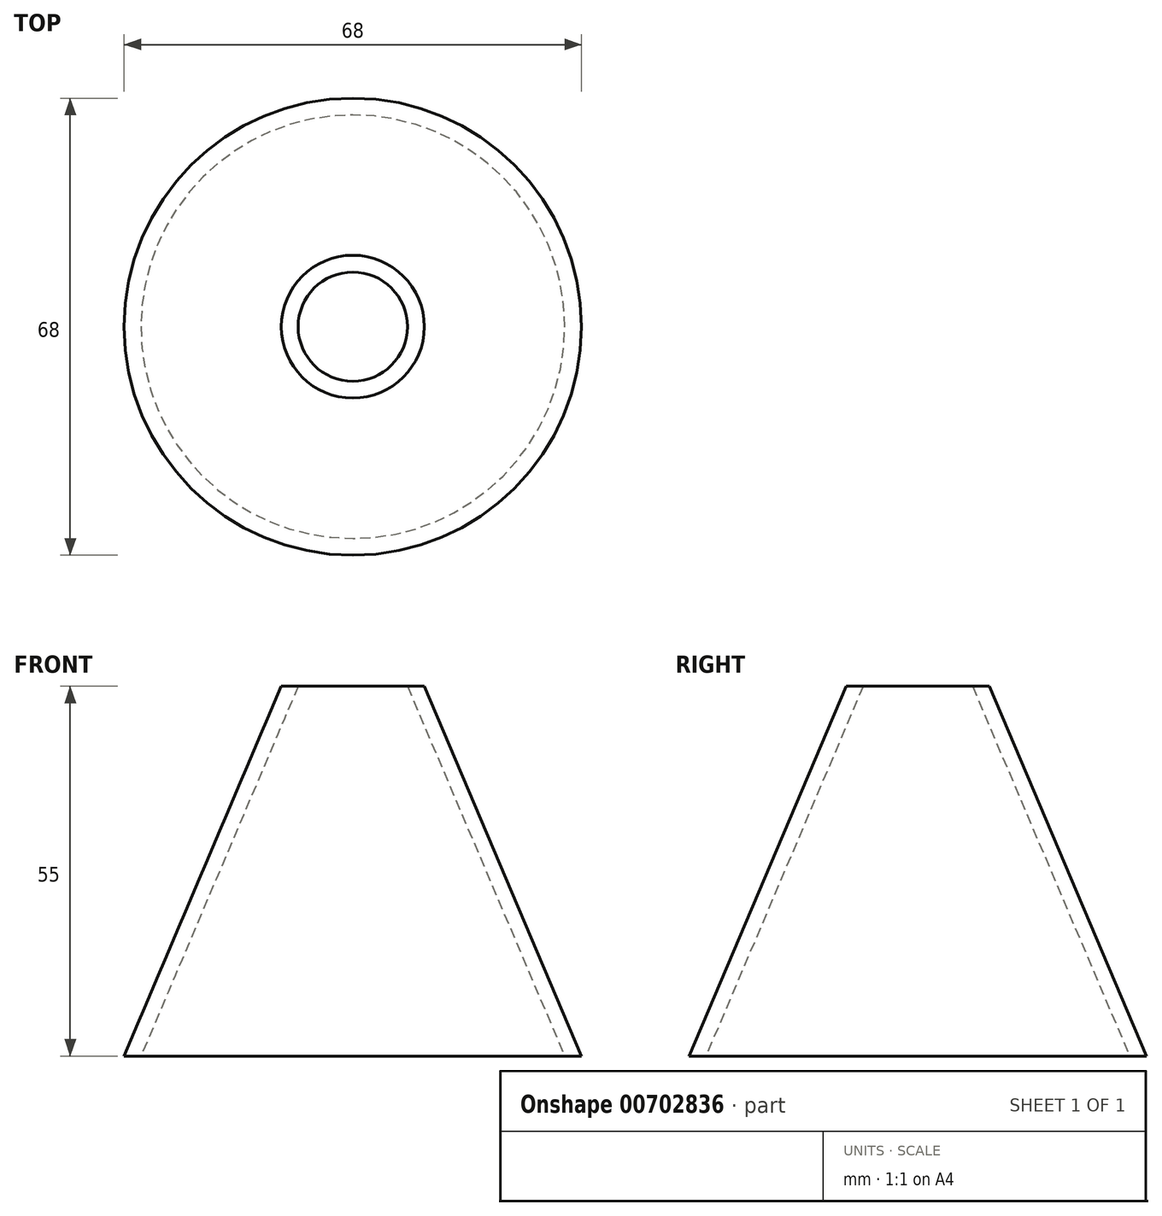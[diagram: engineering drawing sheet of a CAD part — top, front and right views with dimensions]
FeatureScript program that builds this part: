
annotation { "Feature Type Name" : "Feature", "Feature Type Description" : "" }
export const myFeature = defineFeature(function(context is Context, id is Id, definition is map)
    precondition{}
    {
        {
            var Q0;
            Q0=qCreatedBy(makeId("Front.planeOp"),FACE);
            var sketch = newSketch(context, id + "F0", { "sketchPlane" : qUnion([Q0])});
            skLineSegment(sketch, "E0", {"start": v(0, 80) * mm, "end": v(34, 0) * mm});
            skLineSegment(sketch, "E1", {"start": v(0, 80) * mm, "end": v(0, 0) * mm});
            skLineSegment(sketch, "E2", {"start": v(34, 0) * mm, "end": v(0, 0) * mm});
            skLineSegment(sketch, "E3", {"start": v(0, 55) * mm, "end": v(10.62, 55) * mm});
            skLineSegment(sketch, "E4", {"start": v(8.12, 55) * mm, "end": v(31.5, 0) * mm});
            skSolve(sketch);
        }
        {
            var Q0;
            {var subQ5=sQuery(id+"F0.wireOp",EDGE,"E4");Q0=makeQuery(id+"F0.imprint","IMPRINT",FACE,{"disambiguationData":[TD([[makeQuery(id+"F0.imprint","IMPRINT",EDGE,{"derivedFrom":subQ5}),1.0]])]});}
            var Q1;
            Q1=sQuery(id+"F0.wireOp",EDGE,"E1");
            revolve(context, id + "F1", {"surfaceOperationType" : NewSurfaceOperationType.NEW, "entities" : qUnion([Q0]), "axis" : qUnion([Q1]), "revolveType" : RevolveType.FULL, "oppositeDirection" : true});
        }
    });
